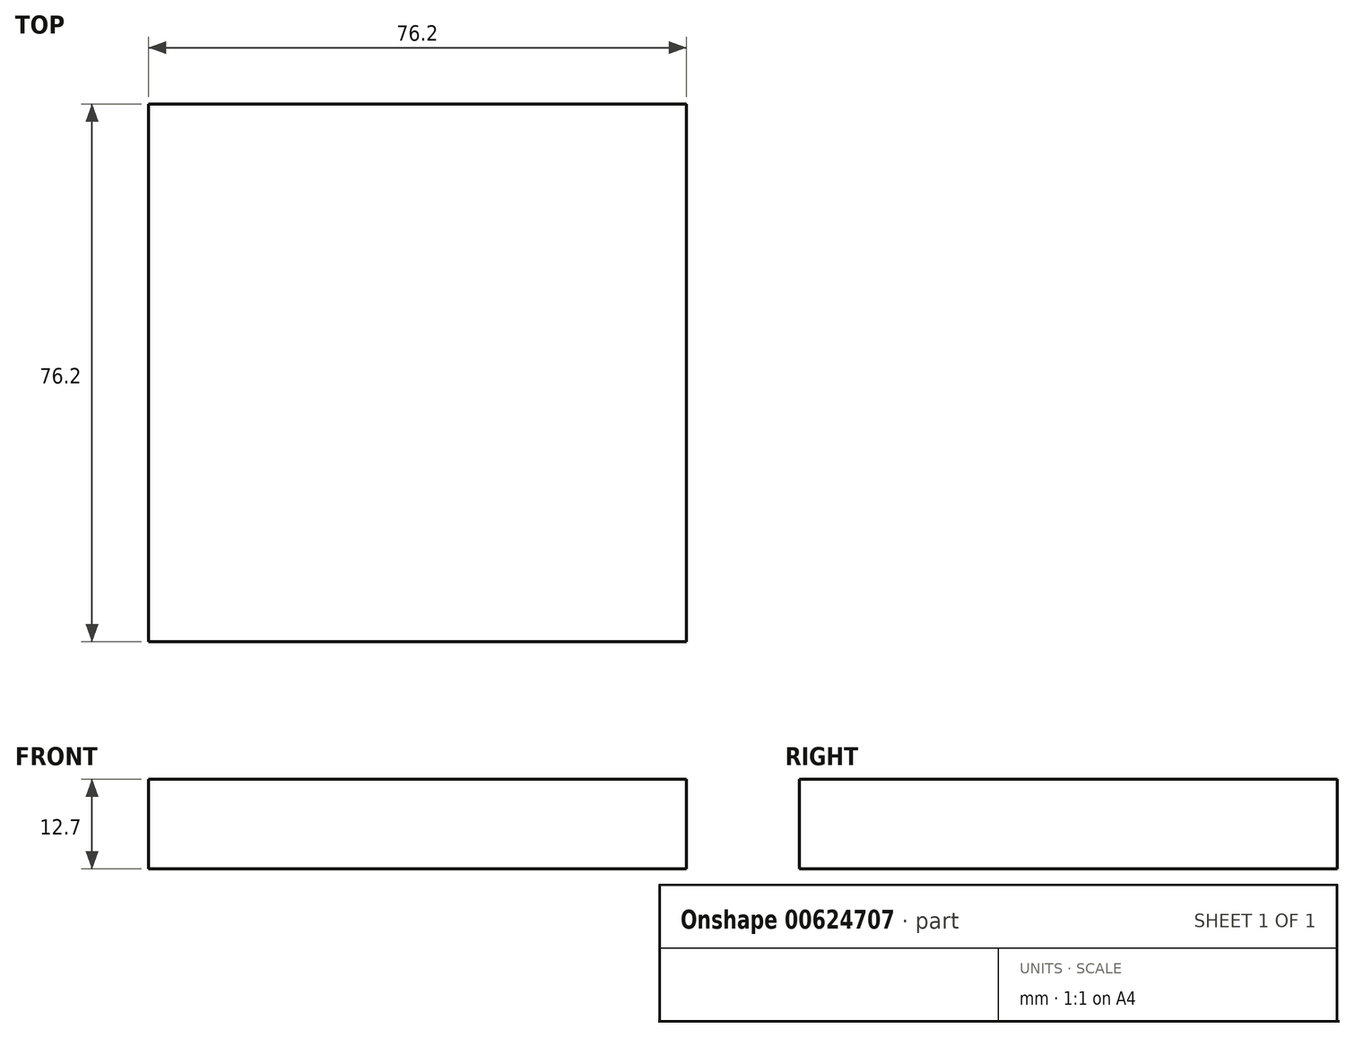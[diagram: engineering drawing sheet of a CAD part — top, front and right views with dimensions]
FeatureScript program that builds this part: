
annotation { "Feature Type Name" : "Feature", "Feature Type Description" : "" }
export const myFeature = defineFeature(function(context is Context, id is Id, definition is map)
    precondition{}
    {
        {
            var Q0;
            Q0=qCreatedBy(makeId("Top.planeOp"),FACE);
            var sketch = newSketch(context, id + "F0", { "sketchPlane" : qUnion([Q0])});
            skLineSegment(sketch, "E0.bottom", {"start": v(38.1, -38.1) * mm, "end": v(-38.1, -38.1) * mm});
            skLineSegment(sketch, "E0.top", {"start": v(38.1, 38.1) * mm, "end": v(-38.1, 38.1) * mm});
            skLineSegment(sketch, "E0.left", {"start": v(38.1, -38.1) * mm, "end": v(38.1, 38.1) * mm});
            skLineSegment(sketch, "E0.right", {"start": v(-38.1, -38.1) * mm, "end": v(-38.1, 38.1) * mm});
            skPoint(sketch, "E0.middle", {"position": v(0, 0) * mm});
            skSolve(sketch);
        }
        {
            var Q0;
            Q0 = qSketchRegion(id + "F0", true);
            extrude(context, id + "F1", {"entities" : qUnion([Q0]), "depth" : 12.7 * mm, "offsetDistance" : 25 * mm});
        }
    });
